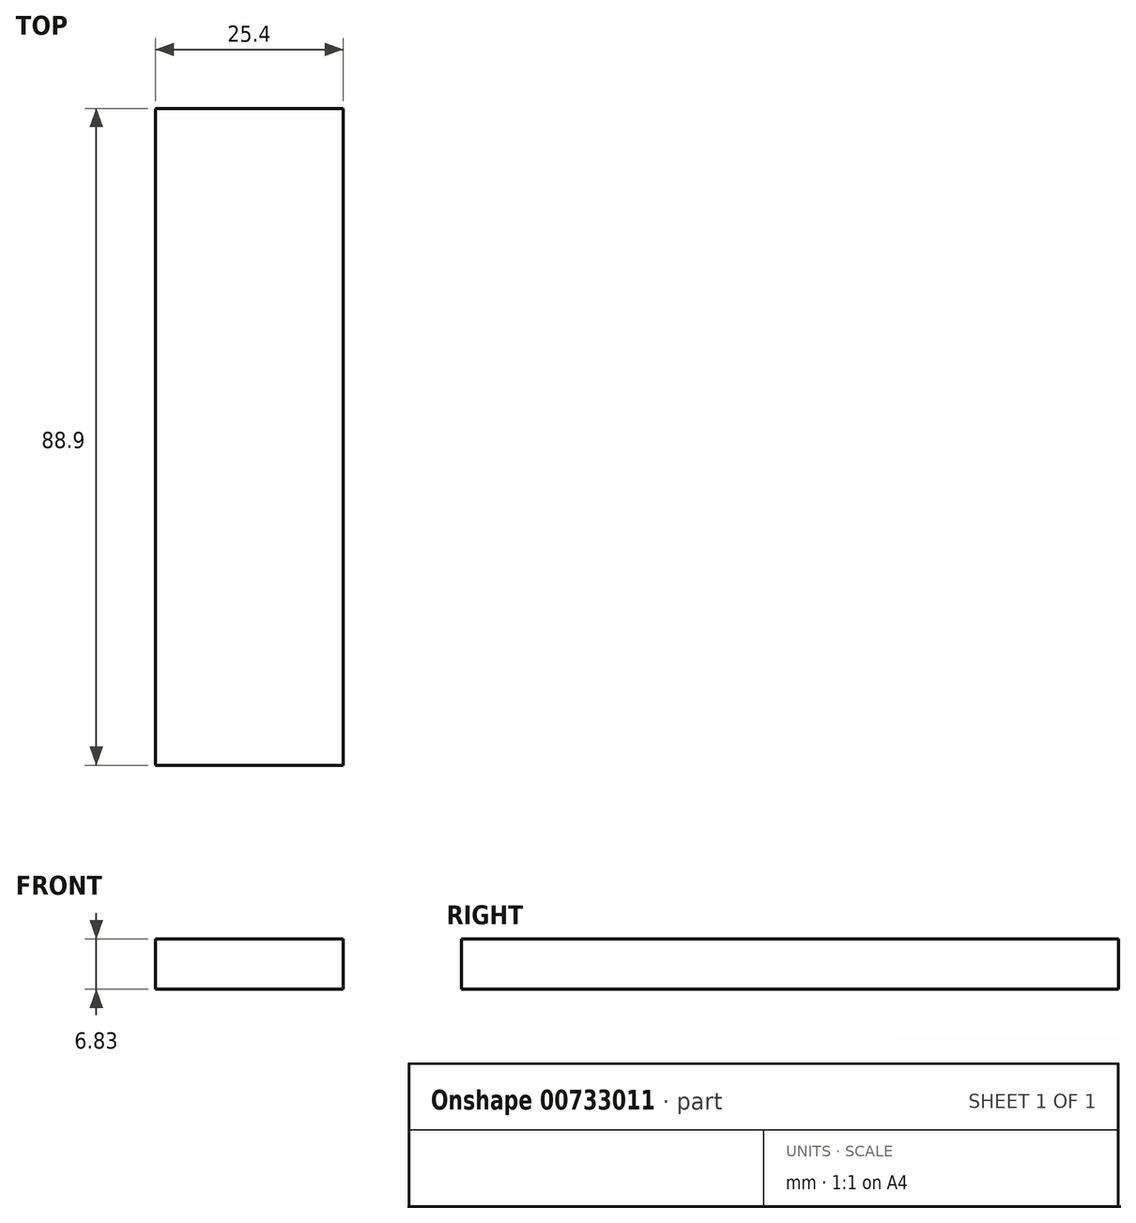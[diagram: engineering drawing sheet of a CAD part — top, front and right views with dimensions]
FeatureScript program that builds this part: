
annotation { "Feature Type Name" : "Feature", "Feature Type Description" : "" }
export const myFeature = defineFeature(function(context is Context, id is Id, definition is map)
    precondition{}
    {
        {
            var Q0;
            Q0=qCreatedBy(makeId("Right.planeOp"),FACE);
            var sketch = newSketch(context, id + "F0", { "sketchPlane" : qUnion([Q0])});
            skLineSegment(sketch, "E0", {"start": v(-41.42, 18.6) * mm, "end": v(47.48, 18.6) * mm});
            skLineSegment(sketch, "E1", {"start": v(47.48, 18.6) * mm, "end": v(47.48, 25.44) * mm});
            skLineSegment(sketch, "E2", {"start": v(47.48, 25.44) * mm, "end": v(-41.42, 25.44) * mm});
            skLineSegment(sketch, "E3", {"start": v(-41.42, 18.6) * mm, "end": v(-41.42, 25.44) * mm});
            skSolve(sketch);
        }
        {
            var Q0;
            Q0=makeQuery(id+"F0.imprint","IMPRINT",FACE,{"disambiguationData":[TD([[makeQuery(id+"F0.imprint","IMPRINT",EDGE,{"derivedFrom":sQuery(id+"F0.wireOp",EDGE,"E0")}),1.0]])]});
            extrude(context, id + "F1", {"entities" : qUnion([Q0]), "endBound" : BoundingType.SYMMETRIC, "depth" : 25.4 * mm, "offsetDistance" : 25.4 * mm});
        }
    });
